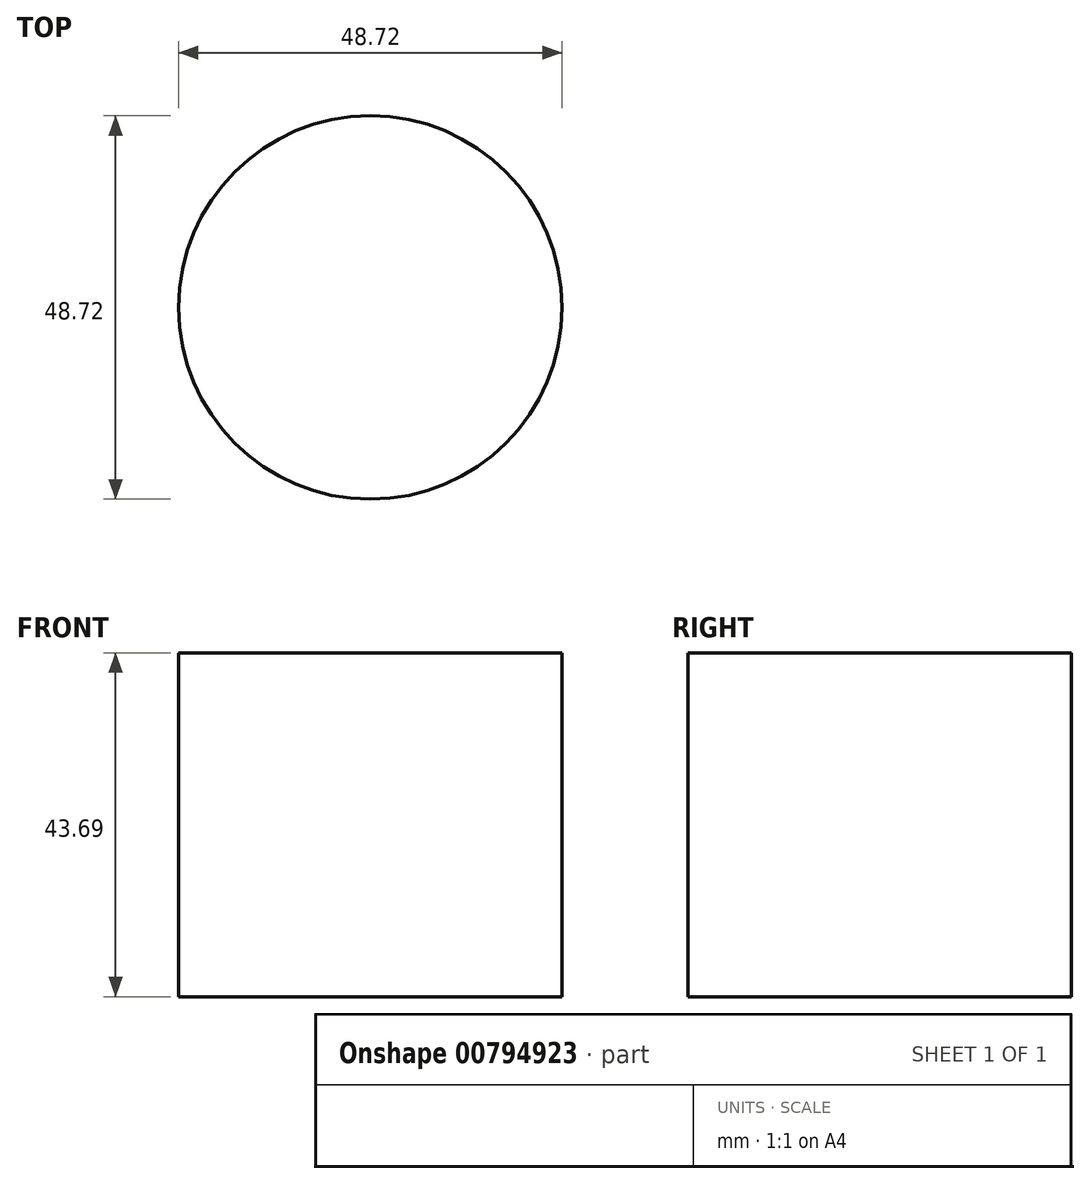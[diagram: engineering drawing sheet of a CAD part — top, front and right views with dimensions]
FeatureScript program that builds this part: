
annotation { "Feature Type Name" : "Feature", "Feature Type Description" : "" }
export const myFeature = defineFeature(function(context is Context, id is Id, definition is map)
    precondition{}
    {
        {
            var Q0;
            Q0=qCreatedBy(makeId("Top.planeOp"),FACE);
            var sketch = newSketch(context, id + "F0", { "sketchPlane" : qUnion([Q0])});
            skCircle(sketch, "E0", {"center": v(0, 0) * mm, "radius": 24.36 * mm});
            skSolve(sketch);
        }
        {
            var Q0;
            Q0 = qSketchRegion(id + "F0", true);
            extrude(context, id + "F1", {"entities" : qUnion([Q0]), "depth" : 43.69 * mm, "offsetDistance" : 25.4 * mm});
        }
    });
